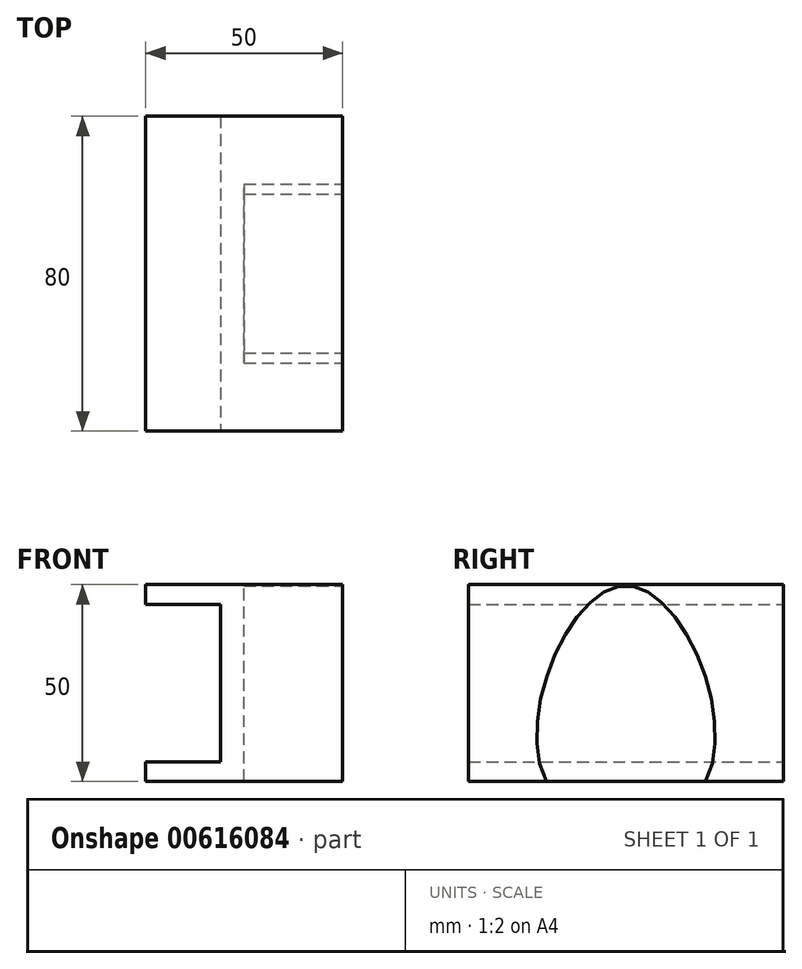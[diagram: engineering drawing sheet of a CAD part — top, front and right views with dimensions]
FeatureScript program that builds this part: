
annotation { "Feature Type Name" : "Feature", "Feature Type Description" : "" }
export const myFeature = defineFeature(function(context is Context, id is Id, definition is map)
    precondition{}
    {
        {
            var Q0;
            Q0=qCreatedBy(makeId("Front.planeOp"),FACE);
            var sketch = newSketch(context, id + "F0", { "sketchPlane" : qUnion([Q0])});
            skLineSegment(sketch, "E0.bottom", {"start": v(25, 25) * mm, "end": v(-25, 25) * mm});
            skLineSegment(sketch, "E0.top", {"start": v(25, -25) * mm, "end": v(-25, -25) * mm});
            skLineSegment(sketch, "E0.left", {"start": v(25, 25) * mm, "end": v(25, -25) * mm});
            skLineSegment(sketch, "E0.right", {"start": v(-25, 25) * mm, "end": v(-25, -25) * mm});
            skSolve(sketch);
        }
        {
            var Q0;
            Q0=makeQuery(id+"F0.imprint","IMPRINT",FACE,{"disambiguationData":[TD([[makeQuery(id+"F0.imprint","IMPRINT",EDGE,{"derivedFrom":sQuery(id+"F0.wireOp",EDGE,"E0.bottom")}),1.0]])]});
            extrude(context, id + "F1", {"entities" : qUnion([Q0]), "endBound" : BoundingType.SYMMETRIC, "depth" : 80 * mm, "offsetDistance" : 25 * mm});
        }
        {
            var Q0;
            Q0=qCreatedBy(makeId("Right.planeOp"),FACE);
            cPlane(context, id + "F2", {"entities" : qUnion([Q0]), "cplaneType" : CPlaneType.OFFSET, "offset" : 25 * mm, "width" : 150 * mm, "height" : 150 * mm});
        }
        {
            var Q0;
            Q0=qCreatedBy(id+"F2.planeOp",FACE);
            var sketch = newSketch(context, id + "F3", { "sketchPlane" : qUnion([Q0])});
            skLineSegment(sketch, "E1", {"start": v(0, 24.67) * mm, "end": v(0, 24.67) * mm});
            skLineSegment(sketch, "E2", {"start": v(0, -25.44) * mm, "end": v(20, -25.44) * mm});
            skLineSegment(sketch, "E3", {"start": v(0, -25.44) * mm, "end": v(-20, -25.44) * mm});
            skFitSpline(sketch, "E4", {"points": [v(-20, -25.44) * mm, v(0, 24.67) * mm, v(20, -25.44) * mm, v(-20, -25.44) * mm]});
            skSolve(sketch);
        }
        {
            var Q0;
            {var subQ0=sQuery(id+"F3.wireOp",EDGE,"E2");Q0=makeQuery(id+"F3.imprint","IMPRINT",FACE,{"disambiguationData":[TD([[makeQuery(id+"F3.imprint","IMPRINT",EDGE,{"derivedFrom":subQ0}),-1.0]])]});}
            var Q1;
            {var subQ0=sQuery(id+"F3.wireOp",EDGE,"E2");Q1=makeQuery(id+"F3.imprint","IMPRINT",FACE,{"disambiguationData":[TD([[makeQuery(id+"F3.imprint","IMPRINT",EDGE,{"derivedFrom":subQ0}),1.0]])]});}
            extrude(context, id + "F4", {"entities" : qUnion([Q0, Q1]), "operationType" : NewBodyOperationType.REMOVE, "oppositeDirection" : true, "depth" : 25 * mm, "offsetDistance" : 25 * mm});
        }
        {
            var Q0;
            Q0=qCreatedBy(makeId("Front.planeOp"),FACE);
            var sketch = newSketch(context, id + "F5", { "sketchPlane" : qUnion([Q0])});
            skLineSegment(sketch, "E5.bottom", {"start": v(-30, 20) * mm, "end": v(-6, 20) * mm});
            skLineSegment(sketch, "E5.top", {"start": v(-30, -20) * mm, "end": v(-6, -20) * mm});
            skLineSegment(sketch, "E5.left", {"start": v(-30, 20) * mm, "end": v(-30, -20) * mm});
            skLineSegment(sketch, "E5.right", {"start": v(-6, 20) * mm, "end": v(-6, -20) * mm});
            skLineSegment(sketch, "E6", {"start": v(-6, 20) * mm, "end": v(-6, 0) * mm});
            skSolve(sketch);
        }
        {
            var Q0;
            Q0 = qSketchRegion(id + "F5", true);
            extrude(context, id + "F6", {"entities" : qUnion([Q0]), "operationType" : NewBodyOperationType.REMOVE, "endBound" : BoundingType.THROUGH_ALL, "oppositeDirection" : true, "depth" : 25 * mm, "offsetDistance" : 25 * mm});
        }
        {
            var Q0;
            Q0 = qSketchRegion(id + "F5", true);
            extrude(context, id + "F7", {"entities" : qUnion([Q0]), "operationType" : NewBodyOperationType.REMOVE, "endBound" : BoundingType.THROUGH_ALL, "depth" : 25 * mm, "offsetDistance" : 25 * mm});
        }
    });
